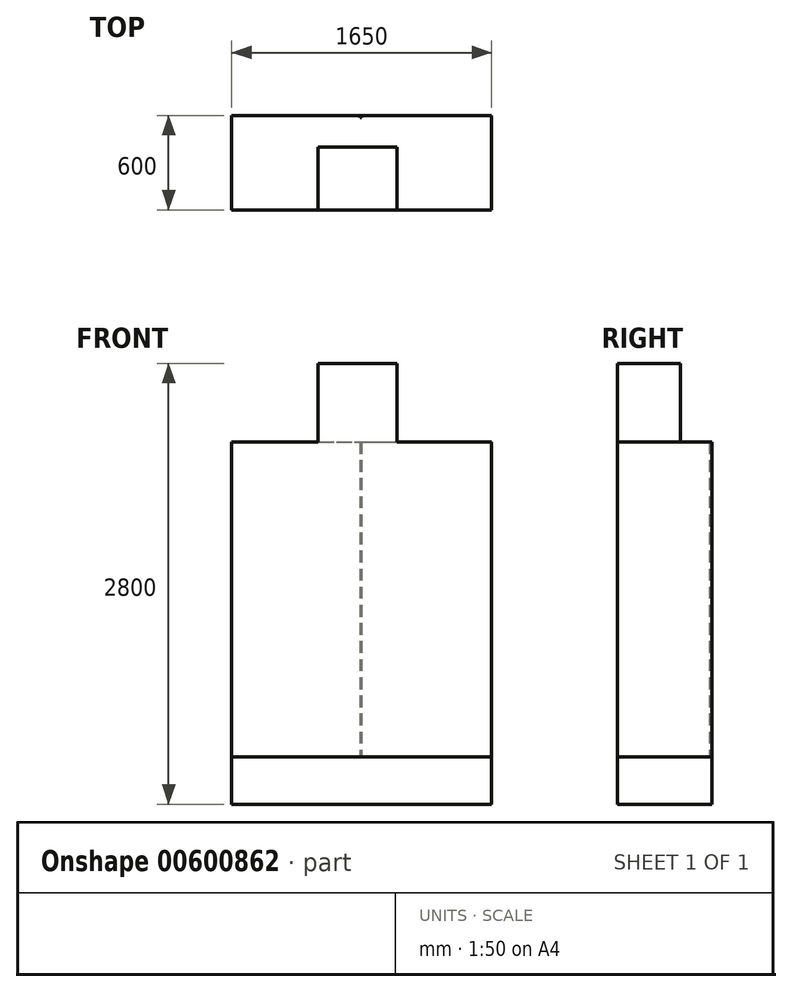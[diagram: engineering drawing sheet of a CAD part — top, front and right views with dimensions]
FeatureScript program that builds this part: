
annotation { "Feature Type Name" : "Feature", "Feature Type Description" : "" }
export const myFeature = defineFeature(function(context is Context, id is Id, definition is map)
    precondition{}
    {
        {
            var Q0;
            Q0=qCreatedBy(makeId("Top.planeOp"),FACE);
            var sketch = newSketch(context, id + "F0", { "sketchPlane" : qUnion([Q0])});
            skLineSegment(sketch, "E0.bottom", {"start": v(0, 0) * mm, "end": v(1650, 0) * mm});
            skLineSegment(sketch, "E0.top", {"start": v(0, 600) * mm, "end": v(1650, 600) * mm});
            skLineSegment(sketch, "E0.left", {"start": v(0, 0) * mm, "end": v(0, 600) * mm});
            skLineSegment(sketch, "E0.right", {"start": v(1650, 0) * mm, "end": v(1650, 600) * mm});
            skSolve(sketch);
        }
        {
            var Q0;
            Q0=makeQuery(id+"F0.imprint","IMPRINT",FACE,{"disambiguationData":[TD([[makeQuery(id+"F0.imprint","IMPRINT",EDGE,{"derivedFrom":sQuery(id+"F0.wireOp",EDGE,"E0.bottom")}),1.0]])]});
            extrude(context, id + "F1", {"entities" : qUnion([Q0]), "depth" : 300 * mm, "offsetDistance" : 25 * mm});
        }
        {
            var Q0;
            Q0=makeQuery(id+"F1.opExtrude","CAP_FACE",FACE,{"disambiguationData":[OSD([sQuery(id+"F0.wireOp",EDGE,"E0.bottom"),sQuery(id+"F0.wireOp",EDGE,"E0.top"),sQuery(id+"F0.wireOp",EDGE,"E0.left"),sQuery(id+"F0.wireOp",EDGE,"E0.right")])],"isStart":false});
            var sketch = newSketch(context, id + "F2", { "sketchPlane" : qUnion([Q0])});
            skLineSegment(sketch, "E1.0", {"start": v(0, 600) * mm, "end": v(1650, 600) * mm});
            skLineSegment(sketch, "E2.0", {"start": v(0, 0) * mm, "end": v(0, 600) * mm});
            skLineSegment(sketch, "E3.0", {"start": v(0, 0) * mm, "end": v(1650, 0) * mm});
            skLineSegment(sketch, "E4.0", {"start": v(1650, 0) * mm, "end": v(1650, 600) * mm});
            skSolve(sketch);
        }
        {
            var Q0;
            Q0=makeQuery(id+"F2.imprint","IMPRINT",FACE,{"disambiguationData":[TD([[makeQuery(id+"F2.imprint","IMPRINT",EDGE,{"derivedFrom":sQuery(id+"F2.wireOp",EDGE,"E1.0")}),-1.0]])]});
            extrude(context, id + "F3", {"entities" : qUnion([Q0]), "depth" : 2000 * mm, "offsetDistance" : 25 * mm});
        }
        {
            var Q0;
            Q0=makeQuery(id+"F3.opExtrude","SWEPT_FACE",FACE,{"disambiguationData":[OSD([sQuery(id+"F2.wireOp",EDGE,"E1.0")])]});
            var sketch = newSketch(context, id + "F4", { "sketchPlane" : qUnion([Q0])});
            skLineSegment(sketch, "E5.bottom", {"start": v(-825, 2300) * mm, "end": v(-815, 2300) * mm});
            skLineSegment(sketch, "E5.top", {"start": v(-825, 300) * mm, "end": v(-815, 300) * mm});
            skLineSegment(sketch, "E5.left", {"start": v(-825, 2300) * mm, "end": v(-825, 300) * mm});
            skLineSegment(sketch, "E5.right", {"start": v(-815, 2300) * mm, "end": v(-815, 300) * mm});
            skSolve(sketch);
        }
        {
            var Q0;
            Q0 = qSketchRegion(id + "F4", true);
            extrude(context, id + "F5", {"entities" : qUnion([Q0]), "operationType" : NewBodyOperationType.REMOVE, "oppositeDirection" : true, "depth" : 15 * mm, "offsetDistance" : 25 * mm});
        }
        {
            var Q0;
            Q0=makeQuery(id+"F3.opExtrude","CAP_FACE",FACE,{"disambiguationData":[OSD([sQuery(id+"F2.wireOp",EDGE,"E1.0"),sQuery(id+"F2.wireOp",EDGE,"E2.0"),sQuery(id+"F2.wireOp",EDGE,"E3.0"),sQuery(id+"F2.wireOp",EDGE,"E4.0")])],"isStart":false});
            var sketch = newSketch(context, id + "F6", { "sketchPlane" : qUnion([Q0])});
            skLineSegment(sketch, "E6.bottom", {"start": v(550, 0) * mm, "end": v(1050, 0) * mm});
            skLineSegment(sketch, "E6.top", {"start": v(550, 400) * mm, "end": v(1050, 400) * mm});
            skLineSegment(sketch, "E6.left", {"start": v(550, 0) * mm, "end": v(550, 400) * mm});
            skLineSegment(sketch, "E6.right", {"start": v(1050, 0) * mm, "end": v(1050, 400) * mm});
            skSolve(sketch);
        }
        {
            var Q0;
            Q0=makeQuery(id+"F6.imprint","IMPRINT",FACE,{"disambiguationData":[TD([[makeQuery(id+"F6.imprint","IMPRINT",EDGE,{"derivedFrom":sQuery(id+"F6.wireOp",EDGE,"E6.bottom")}),1.0]])]});
            extrude(context, id + "F7", {"entities" : qUnion([Q0]), "operationType" : NewBodyOperationType.ADD, "depth" : 500 * mm, "offsetDistance" : 25 * mm});
        }
    });
